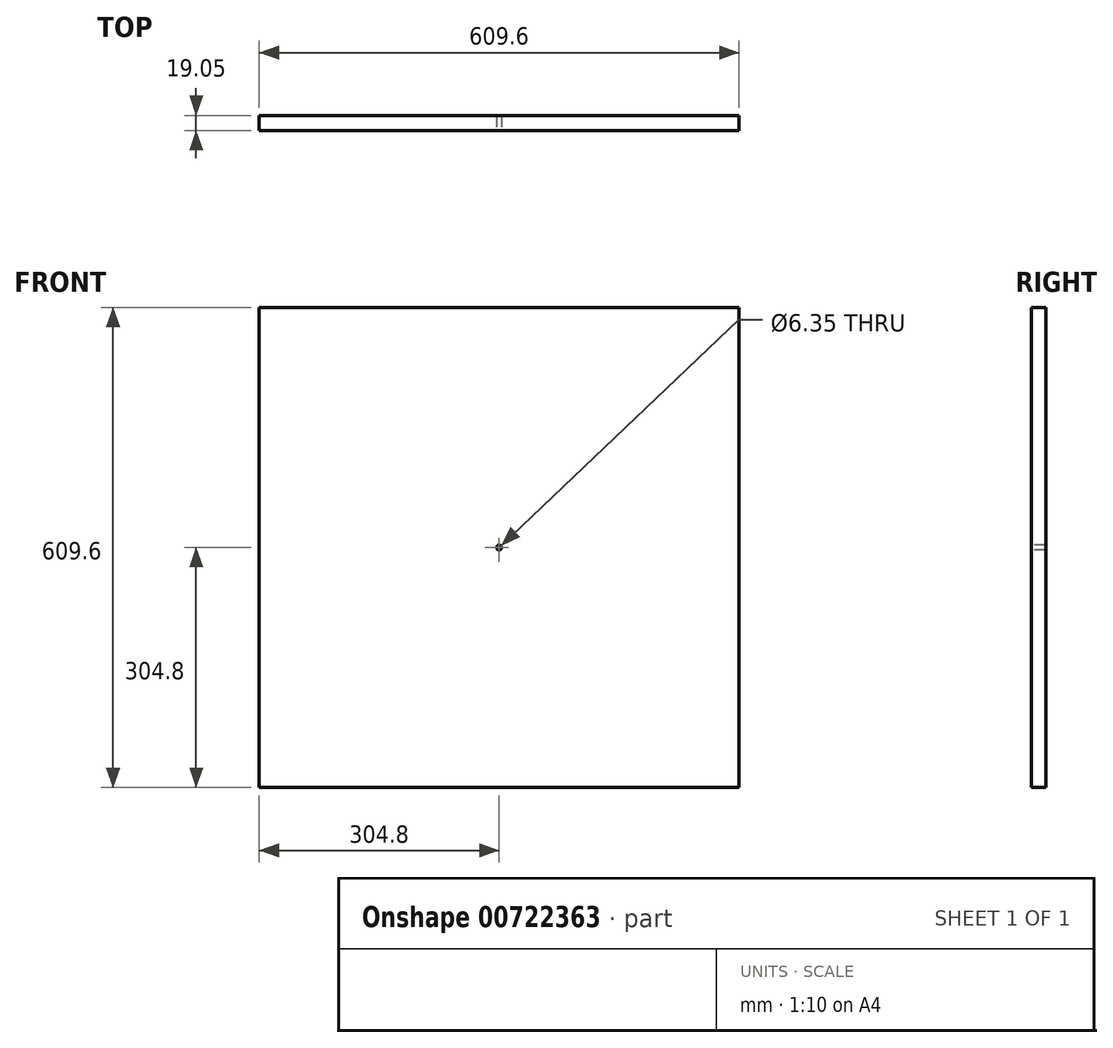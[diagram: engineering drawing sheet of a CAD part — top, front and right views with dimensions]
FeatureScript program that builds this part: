
annotation { "Feature Type Name" : "Feature", "Feature Type Description" : "" }
export const myFeature = defineFeature(function(context is Context, id is Id, definition is map)
    precondition{}
    {
        {
            var Q0;
            Q0=qCreatedBy(makeId("Front.planeOp"),FACE);
            var sketch = newSketch(context, id + "F0", { "sketchPlane" : qUnion([Q0])});
            skLineSegment(sketch, "E0.bottom", {"start": v(0, 0) * mm, "end": v(-609.6, 0) * mm});
            skLineSegment(sketch, "E0.top", {"start": v(0, 609.6) * mm, "end": v(-609.6, 609.6) * mm});
            skLineSegment(sketch, "E0.left", {"start": v(0, 0) * mm, "end": v(0, 609.6) * mm});
            skLineSegment(sketch, "E0.right", {"start": v(-609.6, 0) * mm, "end": v(-609.6, 609.6) * mm});
            skSolve(sketch);
        }
        {
            var Q0;
            Q0=makeQuery(id+"F0.imprint","IMPRINT",FACE,{"disambiguationData":[TD([[makeQuery(id+"F0.imprint","IMPRINT",EDGE,{"derivedFrom":sQuery(id+"F0.wireOp",EDGE,"E0.bottom")}),-1.0]])]});
            extrude(context, id + "F1", {"entities" : qUnion([Q0]), "depth" : 19.05 * mm, "offsetDistance" : 25.4 * mm});
        }
        {
            var Q0;
            Q0=makeQuery(id+"F1.opExtrude","CAP_FACE",FACE,{"disambiguationData":[OSD([sQuery(id+"F0.wireOp",EDGE,"E0.bottom"),sQuery(id+"F0.wireOp",EDGE,"E0.top"),sQuery(id+"F0.wireOp",EDGE,"E0.left"),sQuery(id+"F0.wireOp",EDGE,"E0.right")])],"isStart":false});
            var sketch = newSketch(context, id + "F2", { "sketchPlane" : qUnion([Q0])});
            skLineSegment(sketch, "E1", {"start": v(-609.6, 304.8) * mm, "end": v(-304.8, 304.8) * mm, "construction": true});
            skLineSegment(sketch, "E2", {"start": v(-304.8, 304.8) * mm, "end": v(-304.8, 609.6) * mm, "construction": true});
            skCircle(sketch, "E3", {"center": v(-304.8, 304.8) * mm, "radius": 3.17 * mm});
            skSolve(sketch);
        }
        {
            var Q0;
            Q0=qSketchRegion(id+"F2",true);
            extrude(context, id + "F3", {"entities" : qUnion([Q0]), "operationType" : NewBodyOperationType.REMOVE, "oppositeDirection" : true, "depth" : 25.4 * mm, "offsetDistance" : 25.4 * mm});
        }
    });
